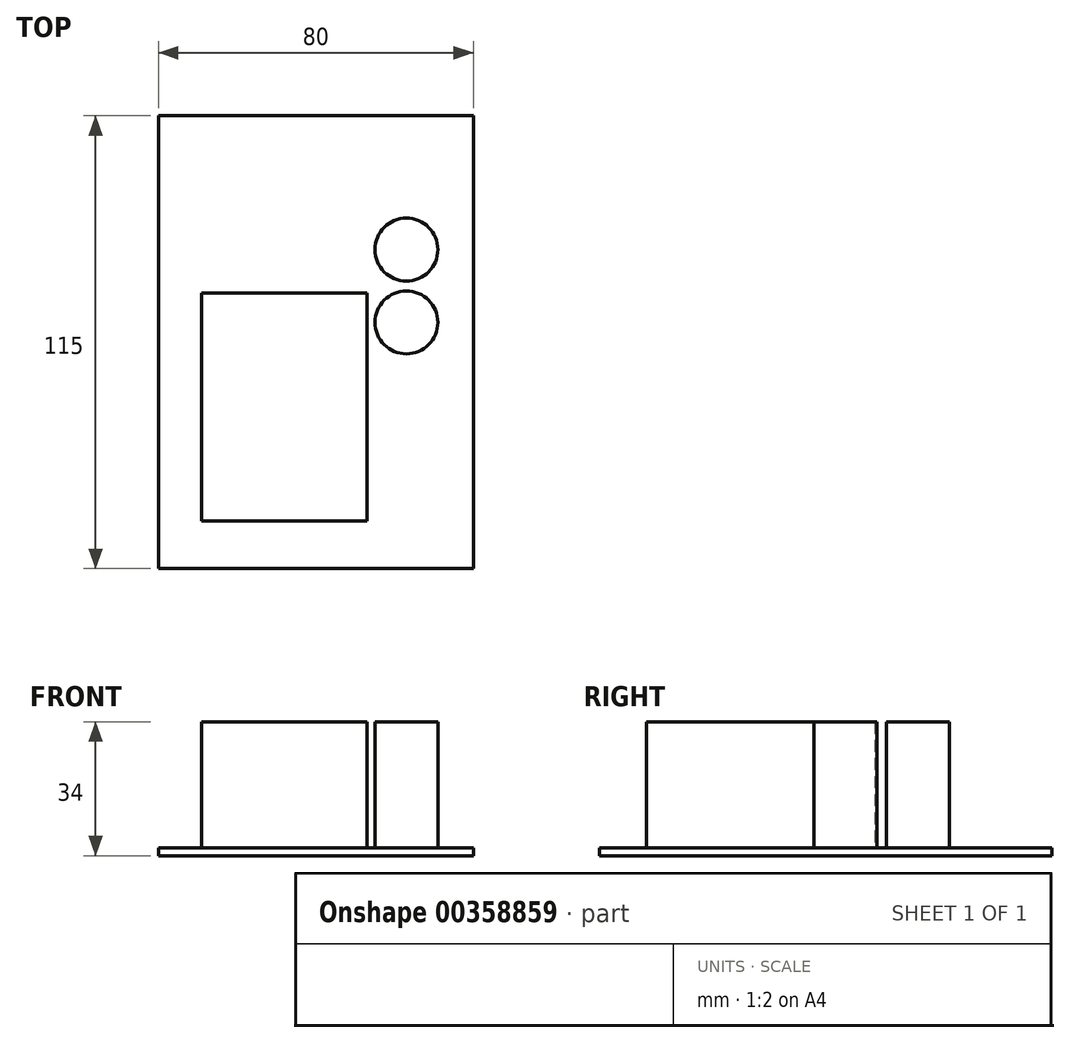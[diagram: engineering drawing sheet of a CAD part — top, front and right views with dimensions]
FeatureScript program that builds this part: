
annotation { "Feature Type Name" : "Feature", "Feature Type Description" : "" }
export const myFeature = defineFeature(function(context is Context, id is Id, definition is map)
    precondition{}
    {
        {
            var Q0;
            Q0=qCreatedBy(makeId("Top.planeOp"),FACE);
            var sketch = newSketch(context, id + "F0", { "sketchPlane" : qUnion([Q0])});
            skLineSegment(sketch, "E0.bottom", {"start": v(-40, -57.5) * mm, "end": v(40, -57.5) * mm});
            skLineSegment(sketch, "E0.top", {"start": v(-40, 57.5) * mm, "end": v(40, 57.5) * mm});
            skLineSegment(sketch, "E0.left", {"start": v(-40, -57.5) * mm, "end": v(-40, 57.5) * mm});
            skLineSegment(sketch, "E0.right", {"start": v(40, -57.5) * mm, "end": v(40, 57.5) * mm});
            skPoint(sketch, "E0.middle", {"position": v(0, 0) * mm});
            skSolve(sketch);
        }
        {
            var Q0;
            Q0 = qSketchRegion(id + "F0", true);
            extrude(context, id + "F1", {"entities" : qUnion([Q0]), "endBound" : BoundingType.SYMMETRIC, "depth" : 2 * mm});
        }
        {
            var Q0;
            Q0=makeQuery(id+"F1.opExtrude","CAP_FACE",FACE,{"disambiguationData":[OSD([sQuery(id+"F0.wireOp",EDGE,"E0.bottom"),sQuery(id+"F0.wireOp",EDGE,"E0.top"),sQuery(id+"F0.wireOp",EDGE,"E0.left"),sQuery(id+"F0.wireOp",EDGE,"E0.right")])],"isStart":false});
            var sketch = newSketch(context, id + "F2", { "sketchPlane" : qUnion([Q0])});
            skLineSegment(sketch, "E1.bottom", {"start": v(13, -45.5) * mm, "end": v(-29, -45.5) * mm});
            skLineSegment(sketch, "E1.top", {"start": v(13, 12.5) * mm, "end": v(-29, 12.5) * mm});
            skLineSegment(sketch, "E1.left", {"start": v(13, -45.5) * mm, "end": v(13, 12.5) * mm});
            skLineSegment(sketch, "E1.right", {"start": v(-29, -45.5) * mm, "end": v(-29, 12.5) * mm});
            skPoint(sketch, "E1.middle", {"position": v(-8, -16.5) * mm});
            skCircle(sketch, "E2", {"center": v(23, 23.5) * mm, "radius": 8 * mm});
            skCircle(sketch, "E3", {"center": v(23, 5) * mm, "radius": 8 * mm});
            skSolve(sketch);
        }
        {
            var Q0;
            Q0 = qSketchRegion(id + "F2", true);
            extrude(context, id + "F3", {"entities" : qUnion([Q0]), "operationType" : NewBodyOperationType.ADD, "depth" : 32 * mm});
        }
    });
